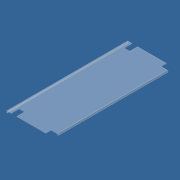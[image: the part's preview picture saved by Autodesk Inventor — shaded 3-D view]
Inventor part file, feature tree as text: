
AUTODESK INVENTOR PART (.ipt)
format: ipt  version: 2012 (Build 160160000, 160)  size: 129,024 bytes
history: native  units: in
note: dims shown in document units (in); Inventor stores cm internally (conversion verified against a paired STEP export)
features: extrude x3, sketch x3
ambient origin geometry x8: Origin, YZ Plane, XZ Plane, XY Plane, X Axis, Y Axis, Z Axis, Center Point
feature tree (6):
  extrude  "Extrusion4"  Depth=1.0in
  extrude  "Extrusion5"  Depth=0.25in
  extrude  "Extrusion6"  Depth=0.175in
  sketch  "Sketch1"  dims[d0=20.0in d1=1.0in]
  sketch  "Sketch4"  dims[d2=0.25in d3=0.25in]
  sketch  "Sketch5"  dims[d26=90.0deg d33=0.175in d35=0.25in d36=0.8589in d37=0.175in d38=0.125in d41=0.67in d42=53.25in d43=0.0in d44=2.5in d45=3.5in d46=2.0in d47=3.5in d48=2.0in d49=2.5in d50=0.5in d51=0.0in d52=3.32in d53=2.375in d55=2.375in d56=3.32in d57=2.0in d58=0.0in]
